# Revit family: Air-Separator_SpiroTop AB thread_Spirotech
name_source: partatom
category: Pipe Accessories
revit_build: Autodesk Revit 2014 (Build: 20140709_2115(x64)
units: mm (PartAtom-declared; Revit-internal decimal feet)

## types (6) — shared parameters
COBie.Type.AssetType = Fixed
COBie.Type.Category = Pipe Accessories
COBie.Type.Constituents = Spirotech air vent
COBie.Type.DurationUnit = Years
COBie.Type.Features = automatic air vents
COBie.Type.Finish = Matt
COBie.Type.Grade = 3
COBie.Type.Length = 52 mm
COBie.Type.Manufacturer = SPIROTECH
COBie.Type.Name = SpiroTop AB
COBie.Type.NominalLength = 52 mm
COBie.Type.NominalWidth = 65 mm  [stored 0.213255 ft]
COBie.Type.Shape = Cylinder
COBie.Type.Size = DN15
COBie.Type.WarrantyDurationUnit = Year
Clash zones = Yes
ClassificationName = Uniclass2015
ClassificationValue = Pr_65_54_93_05
DN = 15 mm
D_2 = 65 mm  [stored 0.213255 ft]
DocumentationCertificates = https://www.spirotech.co.uk
DocumentationInstallationGuide = https://www.spirotech.co.uk
DocumentationLiterature = https://www.spirotech.co.uk
DocumentationTechnical = https://www.spirotech.co.uk
IfcExportAs = ifcFilterType
IfcExportType = WATERFILTER
Loss Method = Not Defined
Manufacturer = Spirotech
Manufacturers Telephone Number = 0208-4513344
Model = SpiroTop AB
NLRS_P_c01_aansluitmethode = Threaded
NominalDepth = 65 mm  [stored 0.213255 ft]
NominalLength = 52 mm
URL = https://www.spirotech.com
connection_diameter = 15 mm
connection_diameter1 = 15 mm
connection_diameter2 = 15 mm
connector_DN = 15 mm
connector_DO = 12.7 mm  [stored 0.0416667 ft]
d = 12.7 mm  [stored 0.0416667 ft]
draadaansluiting = Yes
kernbuis_D65 = Yes
r = 6.35 mm  [stored 0.0208333 ft]
region_index = 1
ring = No
slb = 7 mm  [stored 0.0229659 ft]
slw = 12 mm  [stored 0.0393701 ft]
using_DN = Yes
zero-valued in all types: COBie.Type.Area, COBie.Type.ReplacementCost, Cost

## per-type parameters (varying)
| type | COBie.Type.Color | COBie.Type.Description | COBie.Type.Material | COBie.Type.ModelNumber | COBie.Type.ModelReference | COBie.Type.NominalHeight | COBie.Type.WarrantyDescription | COBie.Type.WarrantyDurationLabor | COBie.Type.WarrantyDurationParts | Description | H1_2 | IfcDescription | NominalHeight | artnr_wnl | artnr_wuk | catalog_code | desc_wnl | desc_wuk | item_description | knelkoppeling | material_2 | product_index | type_index |
| AB050_DN15 | Brass | SpiroTop Brass fix connection | Brass | AB050 | SpiroTop Air Vent 1/2'' | 112 mm  [stored 0.367454 ft] | On all standard Spirotech Brass products with operational temperatures up to 110°C | 20 | 20 | SpiroTop Brass fix connection | 112 mm  [stored 0.367454 ft] | SpiroTop Brass fix connection | 112 mm  [stored 0.367454 ft] | AB050 | AB050 | AB050 | SpiroTop Air Vent 1/2'' | SpiroTop Air Vent 1/2'' | SpiroTop Air Vent 1/2'' | Yes | Spirotech_Brass | 1 | 1 |
| AB050/030_DN15 | Brass | SpiroTop Brass fix connection high pressure | Brass | AB050/030 | SpiroTop Air Vent 1/2'' (16 bar) | 134 mm | On all standard Spirotech Brass products with operational temperatures up to 110°C | 20 | 20 | SpiroTop Brass fix connection high pressure | 134 mm | SpiroTop Brass fix connection high pressure | 134 mm | AB050/030 | AB050/030 | AB050/030 | SpiroTop Air Vent 1/2'' (16 bar) | SpiroTop Air Vent 1/2'' (16 bar) | SpiroTop Air Vent 1/2'' (16 bar) | No | Spirotech_Brass | 2 | 2 |
| AB050/025_DN15 | Brass | SpiroTop Brass fix connection high temperature and high pressure | Brass | AB050/025 | SpiroTop Air Vent 1/2'' (150°C / 25 bar) | 134 mm | On steel products and on brass products with operational temperatures in excess of 110°C | 5 | 5 | SpiroTop Brass fix connection high temperature and high pressure | 134 mm | SpiroTop Brass fix connection high temperature and high pressure | 134 mm | AB050/025 | AB050/025 | AB050/025 | SpiroTop Air Vent 1/2'' (150°C / 25 bar) | SpiroTop Air Vent 1/2'' (150°C / 25 bar) | SpiroTop Air Vent 1/2'' (150°C / 25 bar) | No | Spirotech_Brass | 3 | 3 |
| AB050/R002_DN15 | Stainless Steel | SpiroTop Stainless Steel fix connection high temperature | Stainless Steel | AB050/R002 | SpiroTop Air Vent Stainless steel 1/2'' (180°C) | 112 mm  [stored 0.367454 ft] | On steel products and on brass products with operational temperatures in excess of 110°C | 5 | 5 | SpiroTop Stainless Steel fix connection high temperature | 112 mm  [stored 0.367454 ft] | SpiroTop Stainless Steel fix connection high temperature | 112 mm  [stored 0.367454 ft] | AB050/R002 | AB050/R002 | AB050/R002 | SpiroTop Air Vent Stainless steel 1/2'' (180°C) | SpiroTop Air Vent Stainless steel 1/2'' (180°C) | SpiroTop Air Vent Stainless steel 1/2'' (180°C) | No | Spirotech_Steel_RAL1004 | 4 | 4 |
| AB050/R007_DN15 | Stainless Steel | SpiroTop Stainless Steel fix connection high temperature | Stainless Steel | AB050/R007 | SpiroTop Air Vent Stainless steel 1/2'' (180°C) | 112 mm  [stored 0.367454 ft] | On steel products and on brass products with operational temperatures in excess of 110°C | 5 | 5 | SpiroTop Stainless Steel fix connection high temperature | 112 mm  [stored 0.367454 ft] | SpiroTop Stainless Steel fix connection high temperature | 112 mm  [stored 0.367454 ft] | AB050/R007 | AB050/R007 | AB050/R007 | SpiroTop Air Vent Stainless steel 1/2'' (180°C) | SpiroTop Air Vent Stainless steel 1/2'' (180°C) | SpiroTop Air Vent Stainless steel 1/2'' (180°C) | No | Spirotech_Steel_RAL1004 | 5 | 5 |
| AB050/R004_DN15 | Stainless Steel | SpiroTop Stainless Steel fix connection high temperature and high pressure | Stainless Steel | AB050/R004 | SpiroTop Air Vent Stainless Steel 1/2'' (200°C / 25 bar) | 112 mm  [stored 0.367454 ft] | On steel products and on brass products with operational temperatures in excess of 110°C | 5 | 5 | SpiroTop Stainless Steel fix connection high temperature and high pressure | 112 mm  [stored 0.367454 ft] | SpiroTop Stainless Steel fix connection high temperature and high pressure | 112 mm  [stored 0.367454 ft] | AB050/R004 | AB050/R004 | AB050/R004 | SpiroTop Air Vent Stainless Steel 1/2'' (200°C / 25 bar) | SpiroTop Air Vent Stainless Steel 1/2'' (200°C / 25 bar) | SpiroTop Air Vent Stainless Steel 1/2'' (200°C / 25 bar) | No | Spirotech_Steel_RAL1004 | 6 | 6 |

note: [stored X ft] marks values corroborated as IEEE doubles in the binary element streams (Revit-internal decimal feet)

## geometry (parser evidence)
native form markers: Sweep x7
no freeform markers — native parametric forms only
